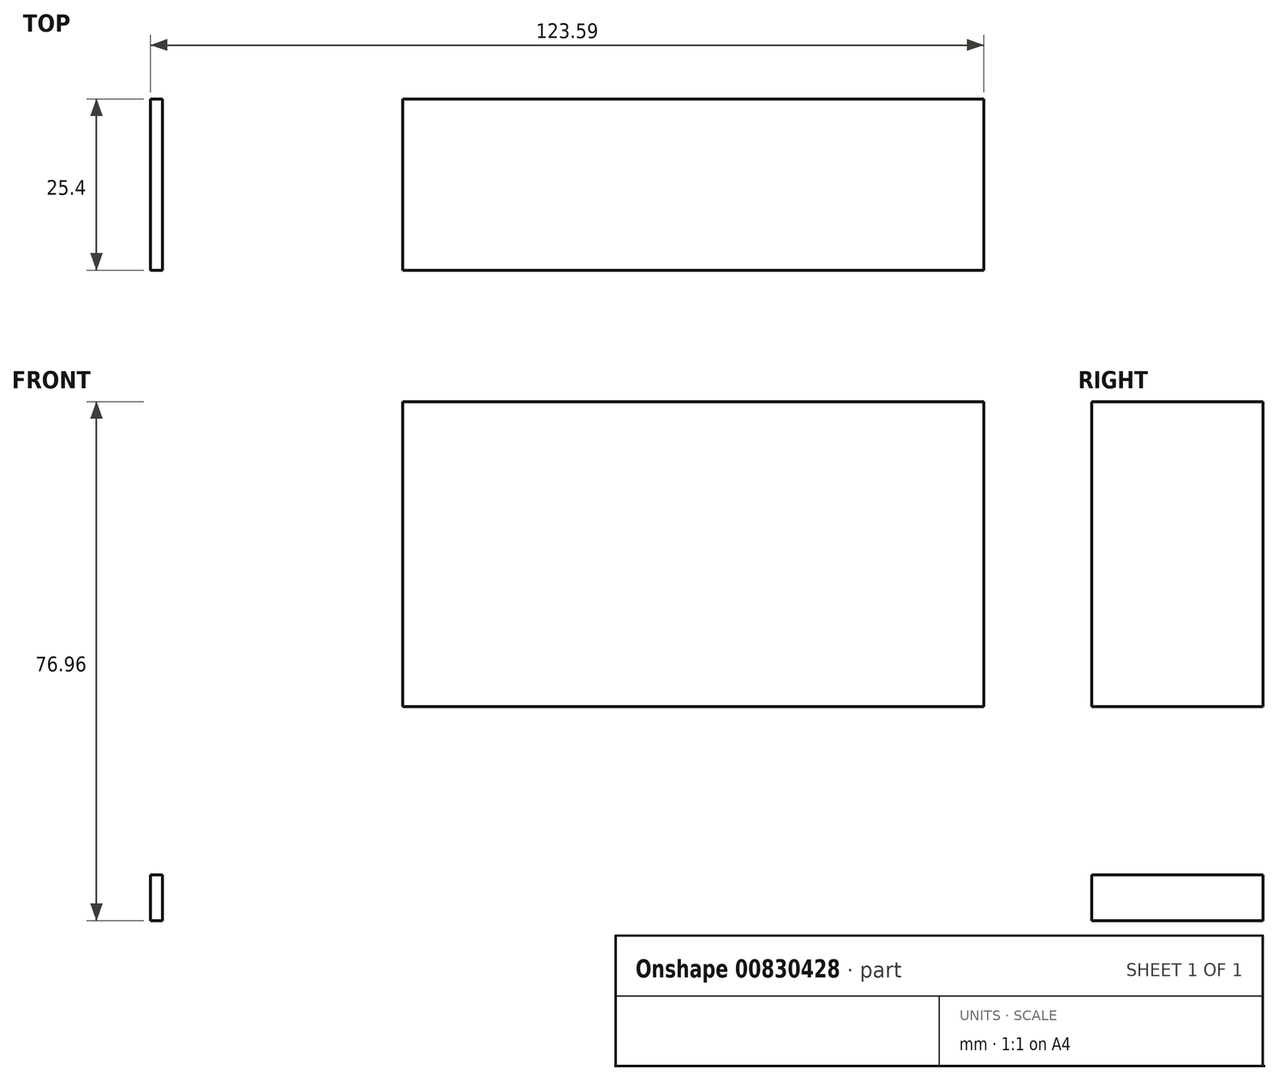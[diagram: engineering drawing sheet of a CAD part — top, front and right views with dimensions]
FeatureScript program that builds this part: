
annotation { "Feature Type Name" : "Feature", "Feature Type Description" : "" }
export const myFeature = defineFeature(function(context is Context, id is Id, definition is map)
    precondition{}
    {
        {
            var Q0;
            Q0=qCreatedBy(makeId("Front.planeOp"),FACE);
            var sketch = newSketch(context, id + "F0", { "sketchPlane" : qUnion([Q0])});
            skLineSegment(sketch, "E0.bottom", {"start": v(-32.66, -53.2) * mm, "end": v(-21.88, -53.2) * mm});
            skLineSegment(sketch, "E0.top", {"start": v(-32.66, -53.2) * mm, "end": v(-21.88, -53.2) * mm});
            skLineSegment(sketch, "E0.left", {"start": v(-32.66, -53.2) * mm, "end": v(-32.66, -53.2) * mm});
            skLineSegment(sketch, "E0.right", {"start": v(-21.88, -53.2) * mm, "end": v(-21.88, -53.2) * mm});
            skLineSegment(sketch, "E1.bottom", {"start": v(-37.4, -24.9) * mm, "end": v(-35.6, -24.9) * mm});
            skLineSegment(sketch, "E1.top", {"start": v(-37.4, -31.7) * mm, "end": v(-35.6, -31.7) * mm});
            skLineSegment(sketch, "E1.left", {"start": v(-37.4, -24.9) * mm, "end": v(-37.4, -31.7) * mm});
            skLineSegment(sketch, "E1.right", {"start": v(-35.6, -24.9) * mm, "end": v(-35.6, -31.7) * mm});
            skLineSegment(sketch, "E2.bottom", {"start": v(0, 45.26) * mm, "end": v(86.19, 45.26) * mm});
            skLineSegment(sketch, "E2.top", {"start": v(0, 0) * mm, "end": v(86.19, 0) * mm});
            skLineSegment(sketch, "E2.left", {"start": v(0, 45.26) * mm, "end": v(0, 0) * mm});
            skLineSegment(sketch, "E2.right", {"start": v(86.19, 45.26) * mm, "end": v(86.19, 0) * mm});
            skSolve(sketch);
        }
        {
            var Q0;
            Q0=makeQuery(id+"F0.imprint","IMPRINT",FACE,{"disambiguationData":[TD([[makeQuery(id+"F0.imprint","IMPRINT",EDGE,{"derivedFrom":sQuery(id+"F0.wireOp",EDGE,"E2.bottom")}),-1.0]])]});
            var Q1;
            Q1=makeQuery(id+"F0.imprint","IMPRINT",FACE,{"disambiguationData":[TD([[makeQuery(id+"F0.imprint","IMPRINT",EDGE,{"derivedFrom":sQuery(id+"F0.wireOp",EDGE,"E1.bottom")}),-1.0]])]});
            extrude(context, id + "F1", {"entities" : qUnion([Q0, Q1]), "depth" : 25.4 * mm, "offsetDistance" : 25.4 * mm});
        }
    });
